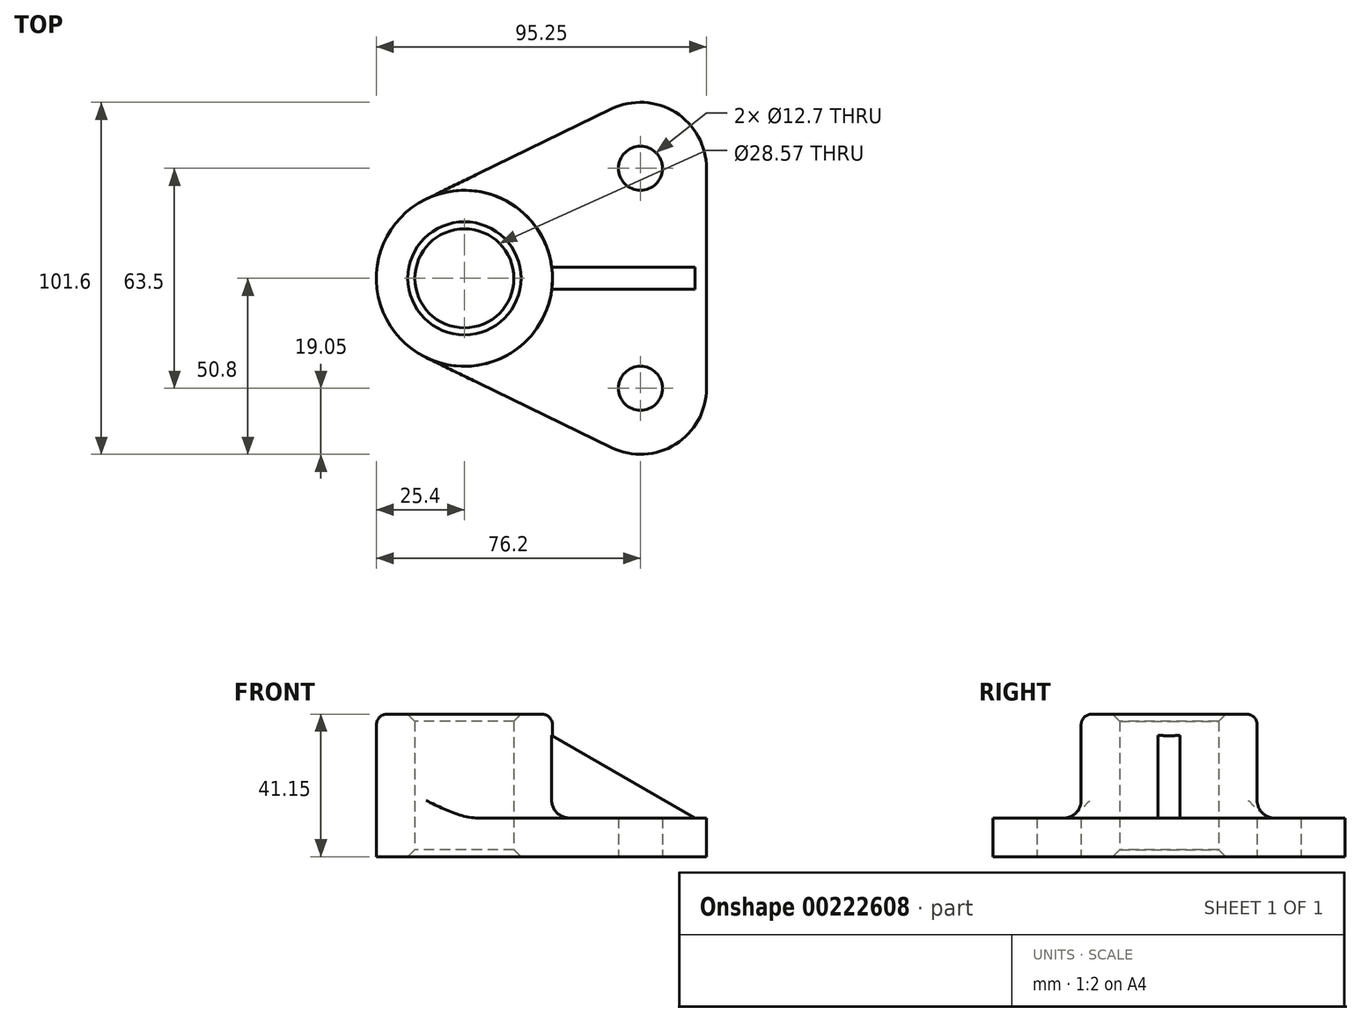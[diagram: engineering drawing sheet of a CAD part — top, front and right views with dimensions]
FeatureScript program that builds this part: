
annotation { "Feature Type Name" : "Feature", "Feature Type Description" : "" }
export const myFeature = defineFeature(function(context is Context, id is Id, definition is map)
    precondition{}
    {
        {
            var Q0;
            Q0=qCreatedBy(makeId("Top.planeOp"),FACE);
            var sketch = newSketch(context, id + "F0", { "sketchPlane" : qUnion([Q0])});
            skCircle(sketch, "E0", {"center": v(0, 0) * mm, "radius": 25.4 * mm});
            skCircle(sketch, "E1", {"center": v(0, 0) * mm, "radius": 14.29 * mm});
            skCircle(sketch, "E2", {"center": v(50.8, 31.75) * mm, "radius": 6.35 * mm});
            skLineSegment(sketch, "E3", {"start": v(-62, 0) * mm, "end": v(120.44, 0) * mm, "construction": true});
            skArc(sketch, "E4", {"start": v(69.85, 31.75) * mm, "mid": v(60.9, 47.9) * mm, "end": v(42.47, 48.88) * mm});
            skLineSegment(sketch, "E5", {"start": v(-11.1, 22.84) * mm, "end": v(42.47, 48.88) * mm});
            skLineSegment(sketch, "E6", {"start": v(69.85, 31.75) * mm, "end": v(69.85, 0) * mm});
            skLineSegment(sketch, "E7", {"start": v(69.85, 0) * mm, "end": v(69.85, -31.75) * mm});
            skCircle(sketch, "E8", {"center": v(50.8, -31.75) * mm, "radius": 6.35 * mm});
            skArc(sketch, "E9", {"start": v(42.47, -48.88) * mm, "mid": v(60.9, -47.9) * mm, "end": v(69.85, -31.75) * mm});
            skLineSegment(sketch, "E10", {"start": v(-11.1, -22.84) * mm, "end": v(42.47, -48.88) * mm});
            skSolve(sketch);
        }
        {
            var Q0;
            Q0=makeQuery(id+"F0.imprint","IMPRINT",FACE,{"disambiguationData":[TD([[makeQuery(id+"F0.imprint","IMPRINT",EDGE,{"derivedFrom":sQuery(id+"F0.wireOp",EDGE,"E1")}),-1.0]])]});
            extrude(context, id + "F1", {"entities" : qUnion([Q0]), "depth" : 41.15 * mm});
        }
        {
            var Q0;
            Q0 = qSketchRegion(id + "F0", true);
            extrude(context, id + "F2", {"entities" : qUnion([Q0]), "operationType" : NewBodyOperationType.ADD, "depth" : 11.18 * mm});
        }
        {
            var Q0;
            Q0=makeQuery(id+"F1.opExtrude","CAP_FACE",FACE,{"disambiguationData":[OSD([sQuery(id+"F0.wireOp",EDGE,"E0"),sQuery(id+"F0.wireOp",EDGE,"E1")])],"isStart":false});
            var sketch = newSketch(context, id + "F3", { "sketchPlane" : qUnion([Q0])});
            skArc(sketch, "E11.0", {"start": v(25.2, -3.18) * mm, "mid": v(25.4, 0) * mm, "end": v(25.2, 3.17) * mm});
            skLineSegment(sketch, "E12", {"start": v(25.4, 0) * mm, "end": v(84.59, 0) * mm});
            skLineSegment(sketch, "E13.bottom", {"start": v(25.2, 3.18) * mm, "end": v(66.55, 3.18) * mm});
            skLineSegment(sketch, "E13.top", {"start": v(25.2, -3.17) * mm, "end": v(66.55, -3.17) * mm});
            skLineSegment(sketch, "E13.right", {"start": v(66.55, 3.18) * mm, "end": v(66.55, -3.17) * mm});
            skPoint(sketch, "E13.middle", {"position": v(45.87, 0) * mm});
            skSolve(sketch);
        }
        {
            var Q0;
            Q0 = qSketchRegion(id + "F3", true);
            extrude(context, id + "F4", {"entities" : qUnion([Q0]), "operationType" : NewBodyOperationType.ADD, "endBound" : BoundingType.UP_TO_NEXT, "oppositeDirection" : true, "depth" : 25.4 * mm});
        }
        {
            var Q0;
            Q0=makeQuery(id+"F4.opExtrude","SWEPT_FACE",FACE,{"disambiguationData":[OSD([sQuery(id+"F3.wireOp",EDGE,"E13.top")])]});
            var sketch = newSketch(context, id + "F5", { "sketchPlane" : qUnion([Q0])});
            skLineSegment(sketch, "E14", {"start": v(66.55, 11.18) * mm, "end": v(25.2, 35.05) * mm});
            skLineSegment(sketch, "E15", {"start": v(66.55, 11.18) * mm, "end": v(45.87, 11.18) * mm});
            skLineSegment(sketch, "E16", {"start": v(66.55, 11.18) * mm, "end": v(66.55, 41.15) * mm});
            skLineSegment(sketch, "E17", {"start": v(66.55, 41.15) * mm, "end": v(25.2, 41.15) * mm});
            skLineSegment(sketch, "E18", {"start": v(25.2, 41.15) * mm, "end": v(25.2, 35.05) * mm});
            skSolve(sketch);
        }
        {
            var Q0;
            Q0 = qSketchRegion(id + "F5", true);
            extrude(context, id + "F6", {"entities" : qUnion([Q0]), "operationType" : NewBodyOperationType.REMOVE, "endBound" : BoundingType.UP_TO_NEXT, "oppositeDirection" : true, "depth" : 25.4 * mm});
        }
        {
            var Q0;
            Q0=makeQuery(id+"F1.opExtrude","CAP_EDGE",EDGE,{"disambiguationData":[OSD([sQuery(id+"F0.wireOp",EDGE,"E1")])],"isStart":true});
            var Q1;
            Q1=makeQuery(id+"F1.opExtrude","CAP_EDGE",EDGE,{"disambiguationData":[OSD([sQuery(id+"F0.wireOp",EDGE,"E1")])],"isStart":false});
            chamfer(context, id + "F7", {"entities" : qUnion([Q0, Q1]), "chamferType" : ChamferType.OFFSET_ANGLE, "width" : 2.03 * mm, "oppositeDirection" : false, "angle" : 45 * degree, "tangentPropagation" : true});
        }
        {
            var Q0;
            {var subQ0=sQuery(id+"F0.wireOp",EDGE,"E0");var subQ1=makeQuery(id+"F1.opExtrude","SWEPT_FACE",FACE,{"disambiguationData":[OSD([subQ0])]});var subQ2=sQuery(id+"F0.wireOp",EDGE,"E10");var subQ3=makeQuery(id+"F2.opExtrude","CAP_FACE",FACE,{"disambiguationData":[OSD([subQ0,sQuery(id+"F0.wireOp",EDGE,"E1"),sQuery(id+"F0.wireOp",EDGE,"E2"),sQuery(id+"F0.wireOp",EDGE,"E4"),sQuery(id+"F0.wireOp",EDGE,"E5"),sQuery(id+"F0.wireOp",EDGE,"E6"),sQuery(id+"F0.wireOp",EDGE,"E7"),sQuery(id+"F0.wireOp",EDGE,"E8"),sQuery(id+"F0.wireOp",EDGE,"E9"),subQ2])],"isStart":false});Q0=makeQuery(id+"F4.boolean.opBoolean","SPLIT",EDGE,{"disambiguationData":[TD([makeQuery(id+"F2.opExtrude","SWEPT_FACE",FACE,{"disambiguationData":[OSD([subQ2])]})])],"derivedFrom":makeQuery(id+"F2.boolean.opBoolean","INTERSECT",EDGE,{"derivedFrom":[subQ1,subQ3]})});}
            var Q1;
            {var subQ0=sQuery(id+"F0.wireOp",EDGE,"E0");var subQ1=makeQuery(id+"F1.opExtrude","SWEPT_FACE",FACE,{"disambiguationData":[OSD([subQ0])]});var subQ2=sQuery(id+"F0.wireOp",EDGE,"E5");var subQ3=makeQuery(id+"F2.opExtrude","CAP_FACE",FACE,{"disambiguationData":[OSD([subQ0,sQuery(id+"F0.wireOp",EDGE,"E1"),sQuery(id+"F0.wireOp",EDGE,"E2"),sQuery(id+"F0.wireOp",EDGE,"E4"),subQ2,sQuery(id+"F0.wireOp",EDGE,"E6"),sQuery(id+"F0.wireOp",EDGE,"E7"),sQuery(id+"F0.wireOp",EDGE,"E8"),sQuery(id+"F0.wireOp",EDGE,"E9"),sQuery(id+"F0.wireOp",EDGE,"E10")])],"isStart":false});Q1=makeQuery(id+"F4.boolean.opBoolean","SPLIT",EDGE,{"disambiguationData":[TD([makeQuery(id+"F2.opExtrude","SWEPT_FACE",FACE,{"disambiguationData":[OSD([subQ2])]})])],"derivedFrom":makeQuery(id+"F2.boolean.opBoolean","INTERSECT",EDGE,{"derivedFrom":[subQ1,subQ3]})});}
            var Q2;
            Q2=makeQuery(id+"F6.boolean.opBoolean","SPLIT",EDGE,{"derivedFrom":makeQuery(id+"F4.opExtrude","SWEPT_EDGE",EDGE,{"disambiguationData":[OSD([sQuery(id+"F0.wireOp",EDGE,"E0"),sQuery(id+"F3.wireOp",EDGE,"E11.0"),sQuery(id+"F3.wireOp",EDGE,"E13.top")])]})});
            var Q3;
            Q3=makeQuery(id+"F6.boolean.opBoolean","SPLIT",EDGE,{"derivedFrom":makeQuery(id+"F4.opExtrude","SWEPT_EDGE",EDGE,{"disambiguationData":[OSD([sQuery(id+"F0.wireOp",EDGE,"E0"),sQuery(id+"F3.wireOp",EDGE,"E11.0"),sQuery(id+"F3.wireOp",EDGE,"E13.bottom")])]})});
            var Q4;
            Q4=makeQuery(id+"F4.opExtrude","CAP_EDGE",EDGE,{"disambiguationData":[OSD([sQuery(id+"F3.wireOp",EDGE,"E13.top")])],"isStart":false});
            var Q5;
            Q5=makeQuery(id+"F4.opExtrude","CAP_EDGE",EDGE,{"disambiguationData":[OSD([sQuery(id+"F3.wireOp",EDGE,"E13.bottom")])],"isStart":false});
            fillet(context, id + "F8", {"entities" : qUnion([Q0, Q1, Q2, Q3, Q4, Q5]), "radius" : 5.08 * mm, "tangentPropagation" : true, "allowEdgeOverflow" : false});
        }
        {
            var Q0;
            Q0=makeQuery(id+"F4.boolean.opBoolean","MERGE",FACE,{"derivedFrom":[makeQuery(id+"F1.opExtrude","CAP_FACE",FACE,{"disambiguationData":[OSD([sQuery(id+"F0.wireOp",EDGE,"E0"),sQuery(id+"F0.wireOp",EDGE,"E1")])],"isStart":false}),makeQuery(id+"F4.opExtrude","CAP_FACE",FACE,{"disambiguationData":[OSD([sQuery(id+"F3.wireOp",EDGE,"E11.0"),sQuery(id+"F3.wireOp",EDGE,"E13.bottom"),sQuery(id+"F3.wireOp",EDGE,"E13.top"),sQuery(id+"F3.wireOp",EDGE,"E13.right")])],"isStart":true})]});
            var sketch = newSketch(context, id + "F9", { "sketchPlane" : qUnion([Q0])});
            skCircle(sketch, "E19", {"center": v(0, 0) * mm, "radius": 25.4 * mm});
            skCircle(sketch, "E20", {"center": v(0, 0) * mm, "radius": 24.28 * mm});
            skSolve(sketch);
        }
        {
            var Q0;
            Q0 = qSketchRegion(id + "F9", true);
            var Q1;
            Q1=makeQuery(id+"F6.boolean.opBoolean","COPY",FACE,{"derivedFrom":makeQuery(id+"F6.opExtrude","SWEPT_FACE",FACE,{"disambiguationData":[OSD([sQuery(id+"F5.wireOp",EDGE,"E14")])]})});
            extrude(context, id + "F10", {"entities" : qUnion([Q0]), "operationType" : NewBodyOperationType.ADD, "endBound" : BoundingType.UP_TO_SURFACE, "oppositeDirection" : true, "endBoundEntityFace" : qUnion([Q1]), "depth" : 25.4 * mm});
        }
        {
            var Q0;
            Q0=makeQuery(id+"F10.boolean.opBoolean","MERGE",EDGE,{"derivedFrom":[makeQuery(id+"F1.opExtrude","CAP_EDGE",EDGE,{"disambiguationData":[OSD([sQuery(id+"F0.wireOp",EDGE,"E0")])],"isStart":false}),makeQuery(id+"F10.opExtrude","CAP_EDGE",EDGE,{"disambiguationData":[OSD([sQuery(id+"F9.wireOp",EDGE,"E19")])],"isStart":true})]});
            fillet(context, id + "F11", {"entities" : qUnion([Q0]), "radius" : 3.05 * mm, "tangentPropagation" : true, "allowEdgeOverflow" : false});
        }
    });
